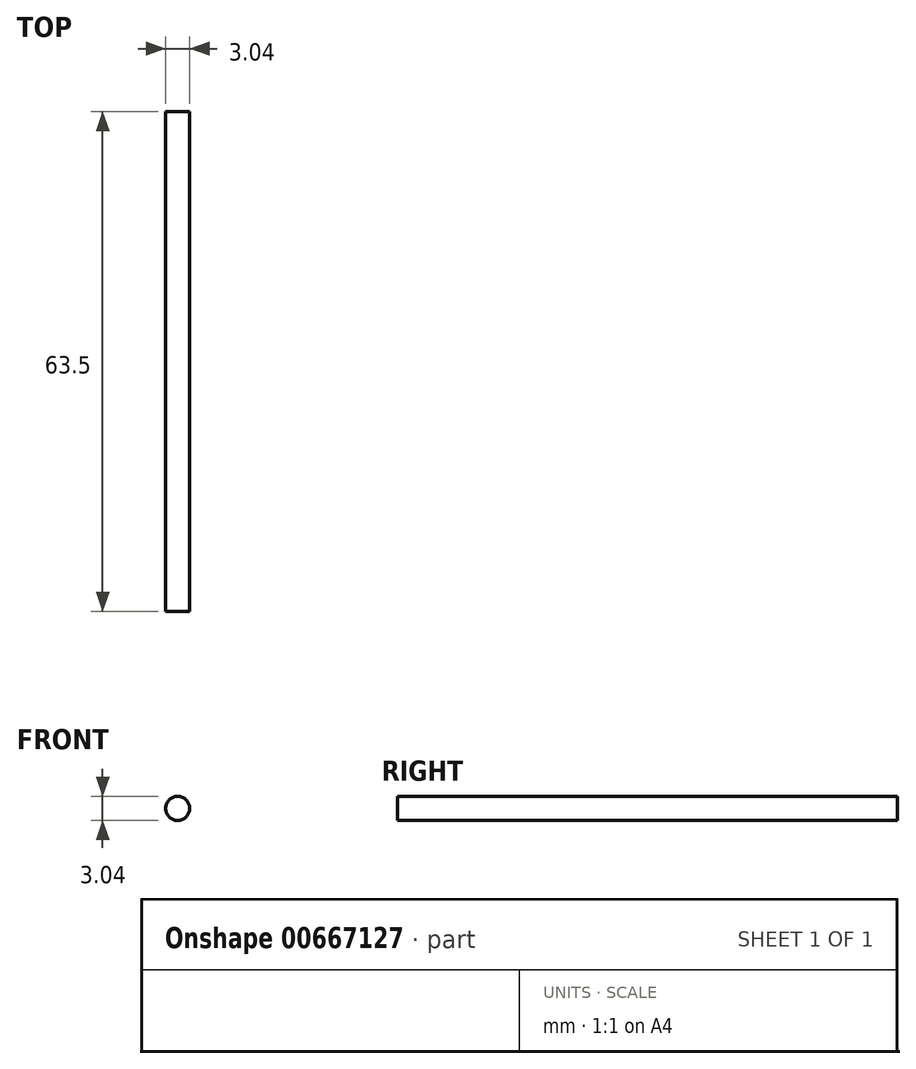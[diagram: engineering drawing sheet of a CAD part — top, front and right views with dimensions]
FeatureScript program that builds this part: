
annotation { "Feature Type Name" : "Feature", "Feature Type Description" : "" }
export const myFeature = defineFeature(function(context is Context, id is Id, definition is map)
    precondition{}
    {
        {
            var Q0;
            Q0=qCreatedBy(makeId("Front.planeOp"),FACE);
            var sketch = newSketch(context, id + "F0", { "sketchPlane" : qUnion([Q0])});
            skCircle(sketch, "E0", {"center": v(0, 0) * mm, "radius": 1.52 * mm});
            skSolve(sketch);
        }
        {
            var Q0;
            Q0=makeQuery(id+"F0.imprint","IMPRINT",FACE,{"disambiguationData":[TD([[makeQuery(id+"F0.imprint","IMPRINT",EDGE,{"derivedFrom":sQuery(id+"F0.wireOp",EDGE,"E0")}),1.0]])]});
            extrude(context, id + "F1", {"entities" : qUnion([Q0]), "oppositeDirection" : true, "depth" : 63.5 * mm, "offsetDistance" : 25.4 * mm});
        }
    });
